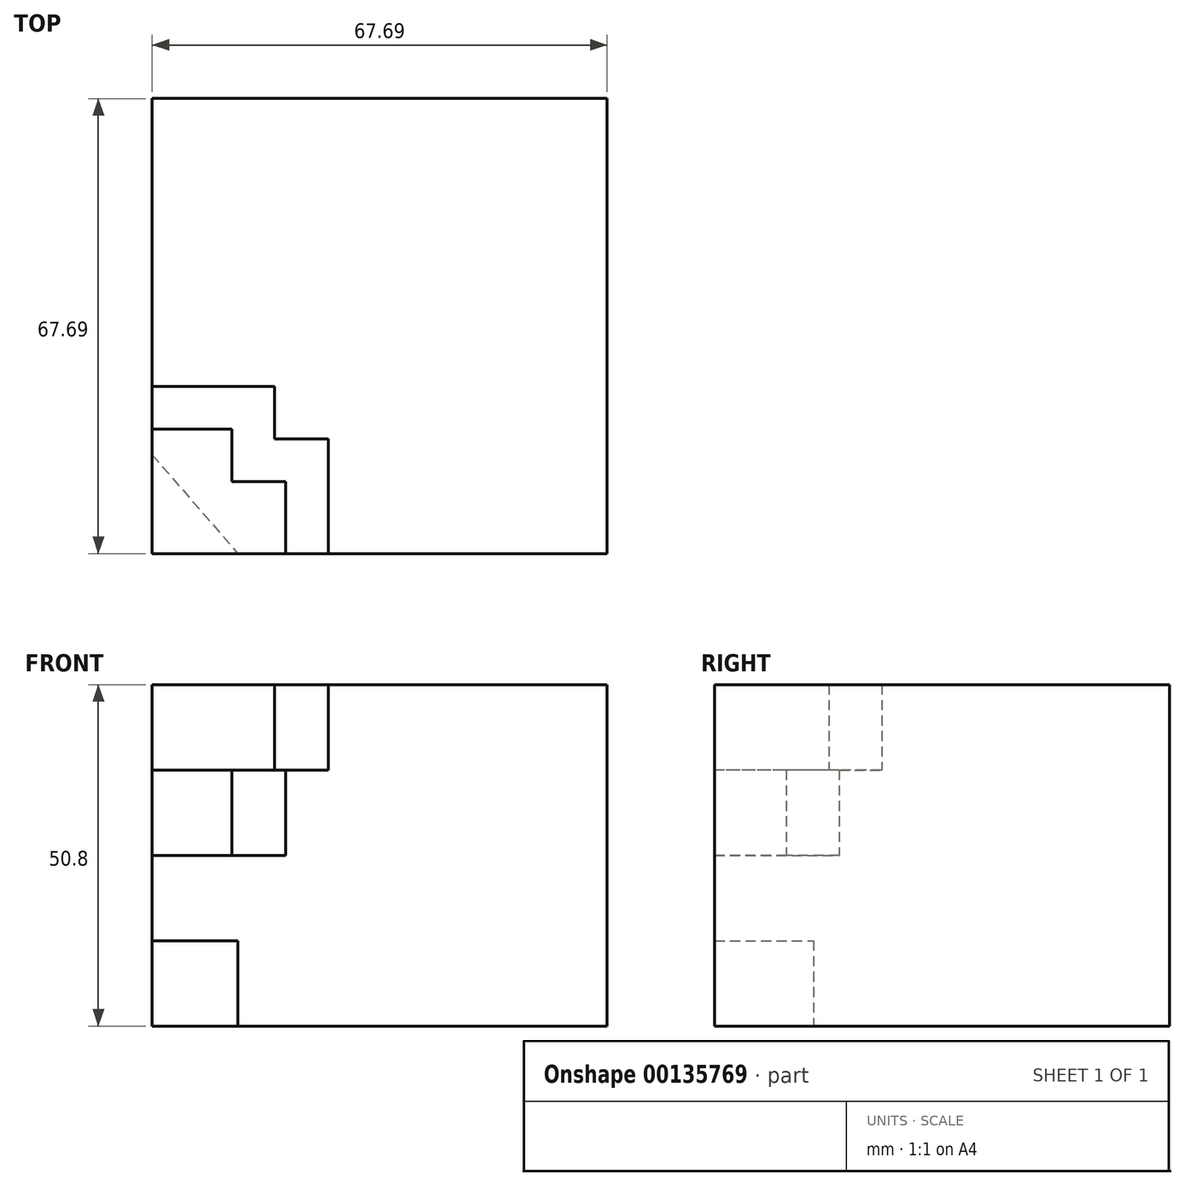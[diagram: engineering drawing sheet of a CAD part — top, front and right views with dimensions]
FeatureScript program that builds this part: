
annotation { "Feature Type Name" : "Feature", "Feature Type Description" : "" }
export const myFeature = defineFeature(function(context is Context, id is Id, definition is map)
    precondition{}
    {
        {
            var Q0;
            Q0=qCreatedBy(makeId("Top.planeOp"),FACE);
            var sketch = newSketch(context, id + "F0", { "sketchPlane" : qUnion([Q0])});
            skLineSegment(sketch, "E0.bottom", {"start": v(12.77, 0) * mm, "end": v(67.7, 0) * mm});
            skLineSegment(sketch, "E0.top", {"start": v(0, 67.7) * mm, "end": v(67.7, 67.7) * mm});
            skLineSegment(sketch, "E0.left", {"start": v(0, 14.69) * mm, "end": v(0, 67.7) * mm});
            skLineSegment(sketch, "E0.right", {"start": v(67.7, 0) * mm, "end": v(67.7, 67.7) * mm});
            skLineSegment(sketch, "E1", {"start": v(0, 14.69) * mm, "end": v(12.77, 0) * mm});
            skSolve(sketch);
        }
        {
            var Q0;
            Q0 = qSketchRegion(id + "F0", true);
            extrude(context, id + "F1", {"entities" : qUnion([Q0]), "depth" : 12.7 * mm});
        }
        {
            var Q0;
            Q0=makeQuery(id+"F1.opExtrude","CAP_FACE",FACE,{"disambiguationData":[OSD([sQuery(id+"F0.wireOp",EDGE,"E0.bottom"),sQuery(id+"F0.wireOp",EDGE,"E0.top"),sQuery(id+"F0.wireOp",EDGE,"E0.left"),sQuery(id+"F0.wireOp",EDGE,"E0.right"),sQuery(id+"F0.wireOp",EDGE,"E1")])],"isStart":false});
            var sketch = newSketch(context, id + "F2", { "sketchPlane" : qUnion([Q0])});
            skLineSegment(sketch, "E2.bottom", {"start": v(0, 0) * mm, "end": v(67.7, 0) * mm});
            skLineSegment(sketch, "E2.top", {"start": v(0, 67.7) * mm, "end": v(67.7, 67.7) * mm});
            skLineSegment(sketch, "E2.left", {"start": v(0, 0) * mm, "end": v(0, 67.7) * mm});
            skLineSegment(sketch, "E2.right", {"start": v(67.7, 0) * mm, "end": v(67.7, 67.7) * mm});
            skSolve(sketch);
        }
        {
            var Q0;
            Q0 = qSketchRegion(id + "F2", true);
            extrude(context, id + "F3", {"entities" : qUnion([Q0]), "operationType" : NewBodyOperationType.ADD, "depth" : 12.7 * mm});
        }
        {
            var Q0;
            Q0=makeQuery(id+"F3.opExtrude","CAP_FACE",FACE,{"disambiguationData":[OSD([sQuery(id+"F2.wireOp",EDGE,"E2.bottom"),sQuery(id+"F2.wireOp",EDGE,"E2.top"),sQuery(id+"F2.wireOp",EDGE,"E2.left"),sQuery(id+"F2.wireOp",EDGE,"E2.right")])],"isStart":false});
            var sketch = newSketch(context, id + "F4", { "sketchPlane" : qUnion([Q0])});
            skLineSegment(sketch, "E3.bottom", {"start": v(0, 67.7) * mm, "end": v(67.7, 67.7) * mm});
            skLineSegment(sketch, "E3.top", {"start": v(19.89, 0) * mm, "end": v(67.7, 0) * mm});
            skLineSegment(sketch, "E3.left", {"start": v(0, 67.7) * mm, "end": v(0, 18.52) * mm});
            skLineSegment(sketch, "E3.right", {"start": v(67.7, 67.7) * mm, "end": v(67.7, 0) * mm});
            skLineSegment(sketch, "E4", {"start": v(0, 18.52) * mm, "end": v(11.86, 18.52) * mm});
            skLineSegment(sketch, "E5", {"start": v(11.86, 18.52) * mm, "end": v(11.86, 10.67) * mm});
            skLineSegment(sketch, "E6", {"start": v(11.86, 10.67) * mm, "end": v(19.89, 10.67) * mm});
            skLineSegment(sketch, "E7", {"start": v(19.89, 10.67) * mm, "end": v(19.89, 0) * mm});
            skSolve(sketch);
        }
        {
            var Q0;
            Q0 = qSketchRegion(id + "F4", true);
            extrude(context, id + "F5", {"entities" : qUnion([Q0]), "operationType" : NewBodyOperationType.ADD, "depth" : 12.7 * mm});
        }
        {
            var Q0;
            Q0=makeQuery(id+"F5.opExtrude","CAP_FACE",FACE,{"disambiguationData":[OSD([sQuery(id+"F4.wireOp",EDGE,"E3.bottom"),sQuery(id+"F4.wireOp",EDGE,"E3.top"),sQuery(id+"F4.wireOp",EDGE,"E3.left"),sQuery(id+"F4.wireOp",EDGE,"E3.right"),sQuery(id+"F4.wireOp",EDGE,"E4"),sQuery(id+"F4.wireOp",EDGE,"E5"),sQuery(id+"F4.wireOp",EDGE,"E6"),sQuery(id+"F4.wireOp",EDGE,"E7")])],"isStart":false});
            var sketch = newSketch(context, id + "F6", { "sketchPlane" : qUnion([Q0])});
            skLineSegment(sketch, "E8.0", {"start": v(26.24, 17.02) * mm, "end": v(26.24, 0) * mm});
            skLineSegment(sketch, "E8.1", {"start": v(18.21, 17.02) * mm, "end": v(26.24, 17.02) * mm});
            skLineSegment(sketch, "E8.2", {"start": v(18.21, 24.87) * mm, "end": v(18.21, 17.02) * mm});
            skLineSegment(sketch, "E8.3", {"start": v(0, 24.87) * mm, "end": v(18.21, 24.87) * mm});
            skLineSegment(sketch, "E9", {"start": v(0, 24.87) * mm, "end": v(0, 67.7) * mm});
            skLineSegment(sketch, "E10", {"start": v(0, 67.7) * mm, "end": v(67.7, 67.7) * mm});
            skLineSegment(sketch, "E11", {"start": v(67.7, 67.7) * mm, "end": v(67.7, 0) * mm});
            skLineSegment(sketch, "E12", {"start": v(67.7, 0) * mm, "end": v(26.24, 0) * mm});
            skSolve(sketch);
        }
        {
            var Q0;
            Q0 = qSketchRegion(id + "F6", true);
            extrude(context, id + "F7", {"entities" : qUnion([Q0]), "operationType" : NewBodyOperationType.ADD, "depth" : 12.7 * mm});
        }
    });
